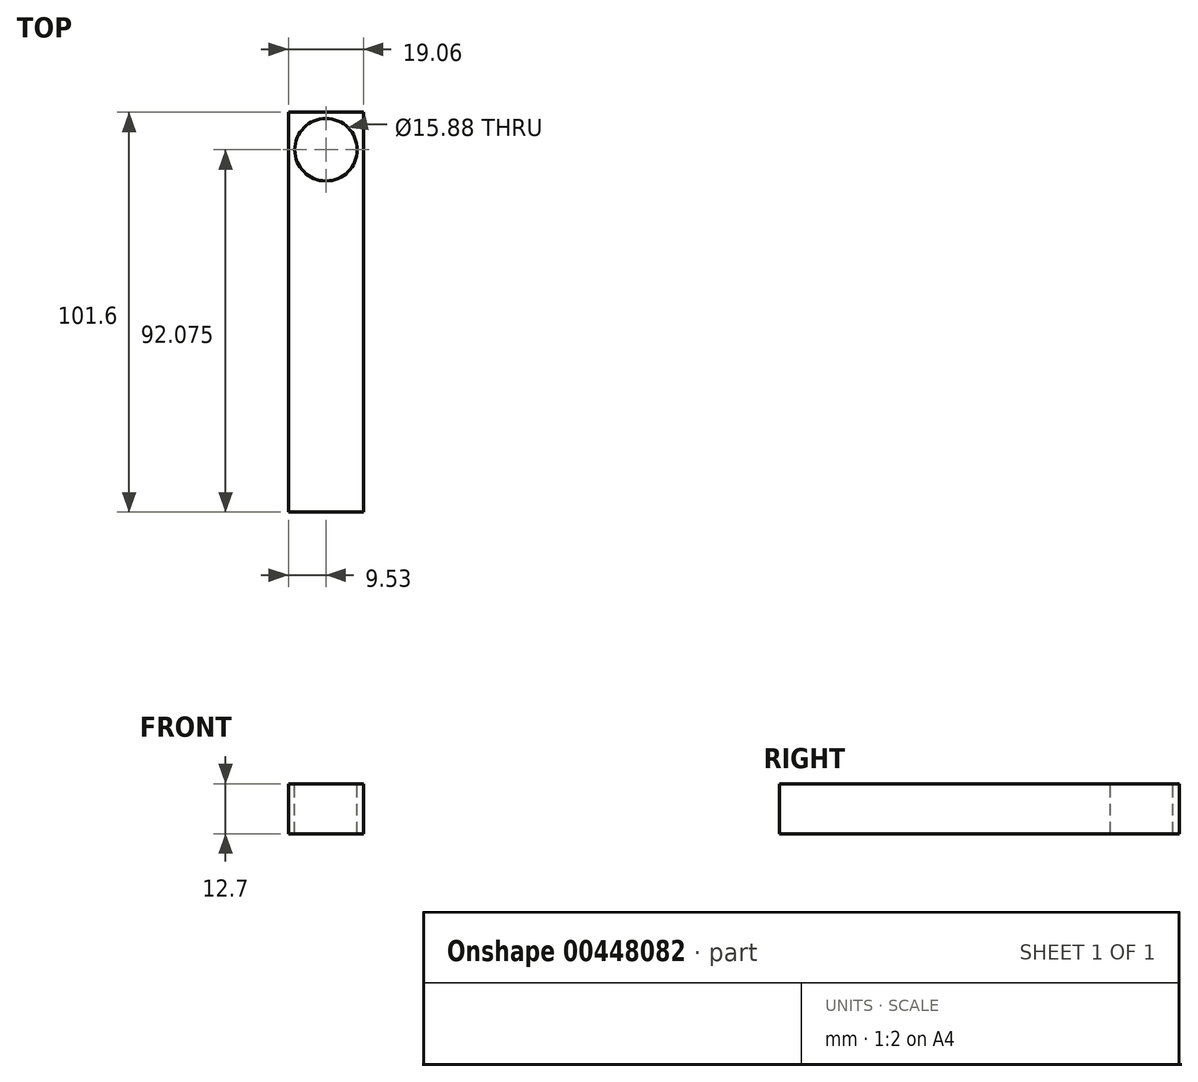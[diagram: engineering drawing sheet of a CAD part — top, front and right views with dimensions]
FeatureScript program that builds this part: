
annotation { "Feature Type Name" : "Feature", "Feature Type Description" : "" }
export const myFeature = defineFeature(function(context is Context, id is Id, definition is map)
    precondition{}
    {
        {
            var Q0;
            Q0=qCreatedBy(makeId("Top.planeOp"),FACE);
            var sketch = newSketch(context, id + "F0", { "sketchPlane" : qUnion([Q0])});
            skLineSegment(sketch, "E0.bottom", {"start": v(-9.53, 50.8) * mm, "end": v(9.53, 50.8) * mm});
            skLineSegment(sketch, "E0.top", {"start": v(-9.53, -50.8) * mm, "end": v(9.53, -50.8) * mm});
            skLineSegment(sketch, "E0.left", {"start": v(-9.53, 50.8) * mm, "end": v(-9.53, -50.8) * mm});
            skLineSegment(sketch, "E0.right", {"start": v(9.53, 50.8) * mm, "end": v(9.53, -50.8) * mm});
            skPoint(sketch, "E0.middle", {"position": v(0, 0) * mm});
            skSolve(sketch);
        }
        {
            var Q0;
            Q0=makeQuery(id+"F0.imprint","IMPRINT",FACE,{"disambiguationData":[TD([[makeQuery(id+"F0.imprint","IMPRINT",EDGE,{"derivedFrom":sQuery(id+"F0.wireOp",EDGE,"E0.bottom")}),-1.0]])]});
            extrude(context, id + "F1", {"entities" : qUnion([Q0]), "depth" : 12.7 * mm});
        }
        {
            var Q0;
            Q0=makeQuery(id+"F1.opExtrude","CAP_FACE",FACE,{"disambiguationData":[OSD([sQuery(id+"F0.wireOp",EDGE,"E0.bottom"),sQuery(id+"F0.wireOp",EDGE,"E0.top"),sQuery(id+"F0.wireOp",EDGE,"E0.left"),sQuery(id+"F0.wireOp",EDGE,"E0.right")])],"isStart":false});
            var sketch = newSketch(context, id + "F2", { "sketchPlane" : qUnion([Q0])});
            skCircle(sketch, "E1", {"center": v(0, 41.28) * mm, "radius": 7.94 * mm});
            skPoint(sketch, "E1.centerSnap0", {"position": v(0, 50.8) * mm});
            skSolve(sketch);
        }
        {
            var Q0;
            Q0 = qSketchRegion(id + "F2", true);
            extrude(context, id + "F3", {"entities" : qUnion([Q0]), "operationType" : NewBodyOperationType.REMOVE, "oppositeDirection" : true, "depth" : 25.4 * mm});
        }
    });
